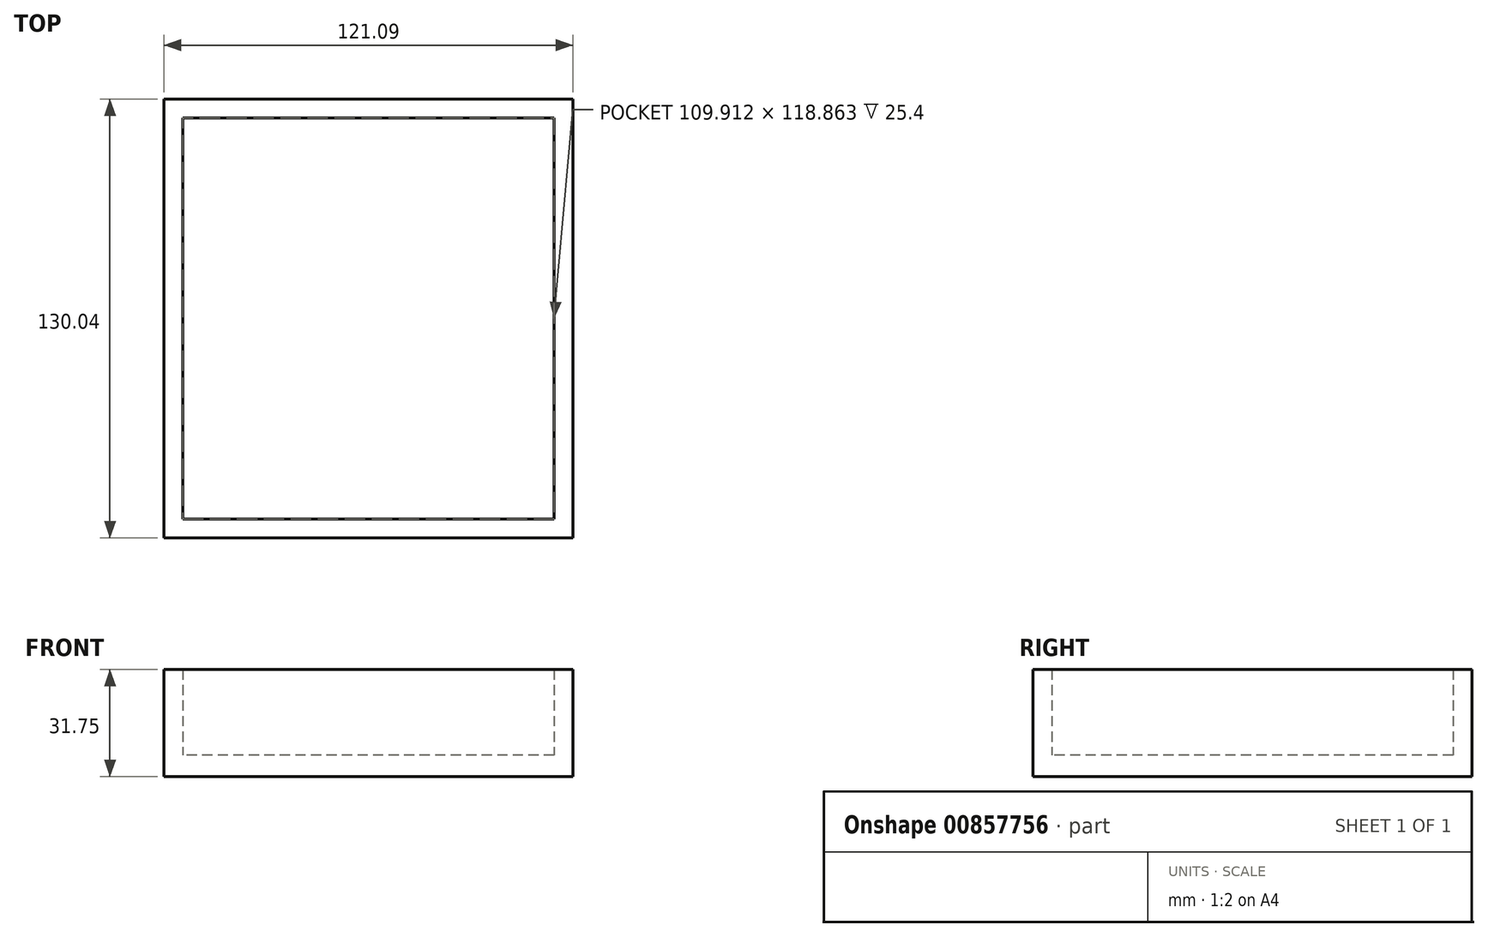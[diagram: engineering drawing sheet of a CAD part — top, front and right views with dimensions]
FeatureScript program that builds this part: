
annotation { "Feature Type Name" : "Feature", "Feature Type Description" : "" }
export const myFeature = defineFeature(function(context is Context, id is Id, definition is map)
    precondition{}
    {
        {
            var Q0;
            Q0=qCreatedBy(makeId("Top.planeOp"),FACE);
            var sketch = newSketch(context, id + "F0", { "sketchPlane" : qUnion([Q0])});
            skLineSegment(sketch, "E0.bottom", {"start": v(-59.62, 63.2) * mm, "end": v(61.47, 63.2) * mm});
            skLineSegment(sketch, "E0.top", {"start": v(-59.62, -66.85) * mm, "end": v(61.47, -66.85) * mm});
            skLineSegment(sketch, "E0.left", {"start": v(-59.62, 63.2) * mm, "end": v(-59.62, -66.85) * mm});
            skLineSegment(sketch, "E0.right", {"start": v(61.47, 63.2) * mm, "end": v(61.47, -66.85) * mm});
            skSolve(sketch);
        }
        {
            var Q0;
            Q0=makeQuery(id+"F0.imprint","IMPRINT",FACE,{"disambiguationData":[TD([[makeQuery(id+"F0.imprint","IMPRINT",EDGE,{"derivedFrom":sQuery(id+"F0.wireOp",EDGE,"E0.bottom")}),-1.0]])]});
            extrude(context, id + "F1", {"entities" : qUnion([Q0]), "depth" : 6.35 * mm, "offsetDistance" : 25.4 * mm});
        }
        {
            var Q0;
            Q0=makeQuery(id+"F1.opExtrude","CAP_FACE",FACE,{"disambiguationData":[OSD([sQuery(id+"F0.wireOp",EDGE,"E0.bottom"),sQuery(id+"F0.wireOp",EDGE,"E0.top"),sQuery(id+"F0.wireOp",EDGE,"E0.left"),sQuery(id+"F0.wireOp",EDGE,"E0.right")])],"isStart":false});
            var sketch = newSketch(context, id + "F2", { "sketchPlane" : qUnion([Q0])});
            skLineSegment(sketch, "E1.0", {"start": v(-54.03, 57.6) * mm, "end": v(-54.03, -61.26) * mm});
            skLineSegment(sketch, "E1.1", {"start": v(55.88, 57.6) * mm, "end": v(-54.03, 57.6) * mm});
            skLineSegment(sketch, "E1.2", {"start": v(55.88, -61.26) * mm, "end": v(55.88, 57.6) * mm});
            skLineSegment(sketch, "E1.3", {"start": v(-54.03, -61.26) * mm, "end": v(55.88, -61.26) * mm});
            skLineSegment(sketch, "E2.0.0", {"start": v(-59.62, 63.2) * mm, "end": v(-59.62, -66.85) * mm});
            skLineSegment(sketch, "E2.0.1", {"start": v(-59.62, -66.85) * mm, "end": v(61.47, -66.85) * mm});
            skLineSegment(sketch, "E2.0.2", {"start": v(61.47, -66.85) * mm, "end": v(61.47, 63.2) * mm});
            skLineSegment(sketch, "E2.0.3", {"start": v(61.47, 63.2) * mm, "end": v(-59.62, 63.2) * mm});
            skSolve(sketch);
        }
        {
            var Q0;
            Q0=makeQuery(id+"F2.imprint","IMPRINT",FACE,{"disambiguationData":[TD([[makeQuery(id+"F2.imprint","IMPRINT",EDGE,{"derivedFrom":sQuery(id+"F2.wireOp",EDGE,"E1.0")}),-1.0]])]});
            extrude(context, id + "F3", {"entities" : qUnion([Q0]), "operationType" : NewBodyOperationType.ADD, "depth" : 25.4 * mm, "offsetDistance" : 25.4 * mm});
        }
    });
